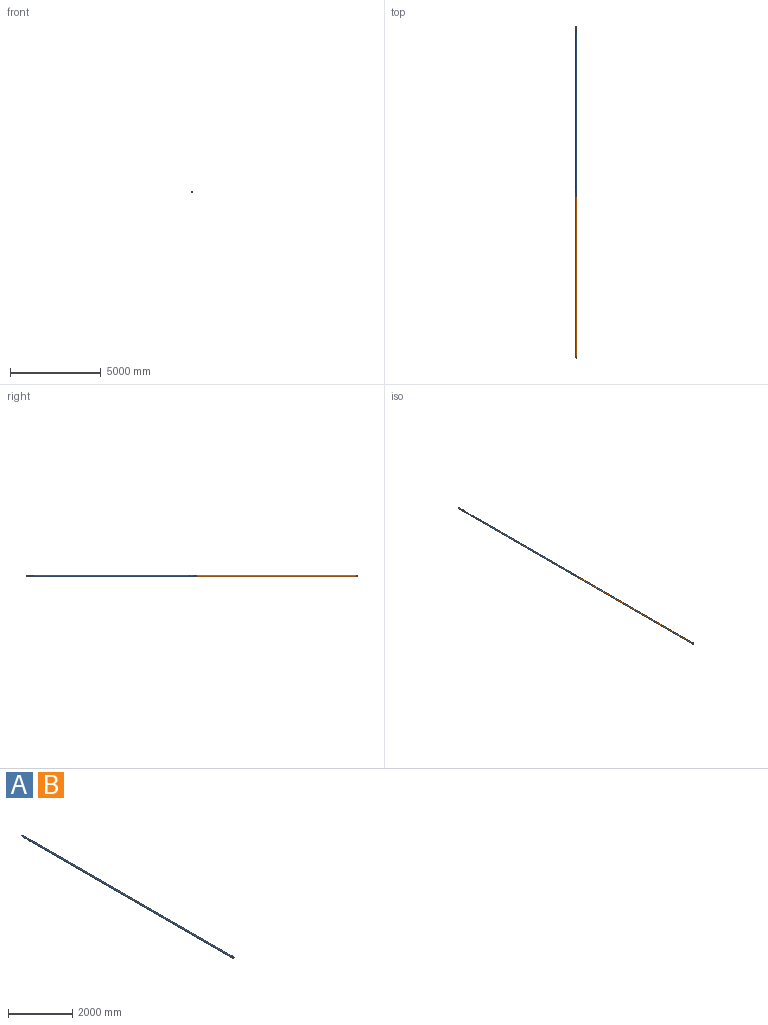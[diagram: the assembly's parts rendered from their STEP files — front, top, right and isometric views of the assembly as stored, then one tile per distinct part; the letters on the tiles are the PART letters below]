
ASSEMBLY  parts=2 mates=1
PART A: 31 faces, bbox 70.1x9321.8x70.1 mm
  f0: cylinder r=24.13mm len=8985.76mm, axis (0,-1,0), area 1362360.1mm2, adj f3,f15
  f1: cylinder r=25.4mm len=65.28mm, axis (0,-1,0), area 10417.9mm2, adj f12,f22
  f2: cylinder r=35.05mm len=70.1mm, axis (0,-1,0), area 727.2mm2, adj f3,f4
  f3: plane 70.1x70.1mm, normal (0,-1,0), area 2030.7mm2, adj f0,f2
  f4: cone r=35.05mm half-angle=70deg, axis (0,-1,0), area 1472.8mm2, adj f2,f5
  f5: cylinder r=28.07mm len=56.15mm, axis (0,-1,0), area 448mm2, adj f4,f6
  f6: plane 56.15x56.15mm, normal (0,1,0), area 261.5mm2, adj f5,f7
  f7: cylinder r=26.55mm len=53.1mm, axis (0,-1,0), area 423.7mm2, adj f6,f8
  f8: plane 53.1x53.1mm, normal (0,1,0), area 187.6mm2, adj f7,f9
  f9: cylinder r=25.4mm len=65.28mm, axis (0,-1,0), area 10417.9mm2, adj f8,f11
  f10: cylinder r=27.94mm len=8837.93mm, axis (0,1,0), area 1551518mm2, adj f11,f13
  f11: plane 55.88x55.88mm, normal (0,-1,0), area 425.6mm2, adj f9,f10
  f12: plane 53.34x53.34mm, normal (0,1,0), area 207.8mm2, adj f1,f13
  f13: torus R=26.67mm, axis (0,1,0), area 344.4mm2, adj f10,f12
  f14: cylinder r=35.05mm len=70.1mm, axis (0,1,0), area 727.2mm2, adj f17,f18
  f15: plane 48.26x48.26mm, normal (0,-1,0), area 187.5mm2, adj f0,f16
  f16: cylinder r=22.86mm len=45.72mm, axis (0,1,0), area 839.1mm2, adj f15,f26
  f17: plane 70.1x70.1mm, normal (0,1,0), area 2030.7mm2, adj f14,f24
  f18: cone r=35.05mm half-angle=70deg, axis (0,1,0), area 1472.8mm2, adj f14,f19
  f19: cylinder r=28.07mm len=56.15mm, axis (0,1,0), area 448mm2, adj f18,f20
  f20: plane 56.15x56.15mm, normal (0,-1,0), area 218.9mm2, adj f19,f21
  f21: cylinder r=26.8mm len=53.61mm, axis (0,1,0), area 427.8mm2, adj f20,f22
  f22: plane 53.61x53.61mm, normal (0,-1,0), area 230.2mm2, adj f1,f21
  f23: cylinder r=10.16mm len=304.8mm, axis (0,-1,0), area 19457.6mm2, adj f26,f30
  f24: cylinder r=24.13mm len=304.8mm, axis (0,-1,0), area 46211.8mm2, adj f17,f25
  f25: plane 48.26x48.26mm, normal (0,1,0), area 1471.7mm2, adj f24,f27
  f26: plane 45.72x45.72mm, normal (0,-1,0), area 1317.4mm2, adj f16,f23
  f27: cylinder r=10.67mm len=25.4mm, axis (0,-1,0), area 1702.5mm2, adj f25,f29
  f28: cylinder r=7.87mm len=25.4mm, axis (0,-1,0), area 1256.6mm2, adj f29,f30
  f29: plane 21.34x21.34mm, normal (0,1,0), area 162.8mm2, adj f27,f28
  f30: plane 20.32x20.32mm, normal (0,-1,0), area 129.5mm2, adj f23,f28
PART B: same geometry as A
PLACE A t=(276.68,165.25,223.17)mm
PLACE B t=(276.68,-8826.35,223.17)mm
MATE fastened A.f0 <-> B.f1  axis (0,1,0) through (276.68,165.25,223.17)mm
